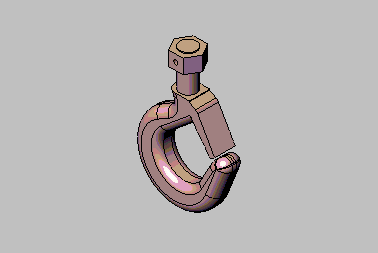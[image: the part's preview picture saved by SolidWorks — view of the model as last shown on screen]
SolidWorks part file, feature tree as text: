
SOLIDWORKS PART (.sldprt)
format: sldprt  version: not decoded by parser v0  size: 1,446,912 bytes
history: native  units: mm
features: plane x5, sketch x4, extrude x3, fillet x2, material x1, mirror x1, cut_extrude x1 (+10 scaffold rows collapsed)
feature tree (27):
  scaffold x10  (default folders/planes/origin — collapsed)
  material  "Material <not specified>"
  plane  "Plane1"  Offset=0mm
  plane  "Plane2"  Offset=0mm
  plane  "Plane3"  Offset=0mm
  sketch  "Sketch1"
  extrude  "Extrude1"  Depth=7.9375mm
  fillet  "Fillet1"  Radius=6.35mm
  fillet  "Fillet2"  Radius=4.7625mm
  mirror  "Mirror1"
  sketch  "Sketch2"  dims[D1=12.7mm]
  extrude  "Extrude2"  Depth=28.575mm
  plane  "Plane4"  Offset=0mm
  plane  "Plane5"  Offset=16.66875mm
  sketch  "Sketch3"  dims[D1=19.05mm]
  extrude  "Extrude3"  Depth=11.1125mm
  sketch  "Sketch4"  dims[D2=3.175mm D1=~5.55625mm]
  cut_extrude  "Cut-Extrude1"  [1 undecoded]
decode coverage: 8 of 11 modeling features carry decoded parameters
note: ~ marks probable driven/reference dimensions
note: 1 parameter value undecoded
note: suppression state not decoded; provenance and decode notes live in map.json
